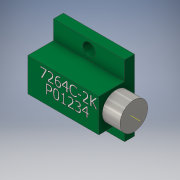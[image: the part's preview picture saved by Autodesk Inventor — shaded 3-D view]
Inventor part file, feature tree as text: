
AUTODESK INVENTOR PART (.ipt)
format: ipt  version: 2016 (Build 200138000, 138)  size: 567,808 bytes
history: native  units: in
note: dims shown in document units (in); Inventor stores cm internally (conversion verified against a paired STEP export)
features: sketch x6, extrude x3, emboss x1, other x1
ambient origin geometry x8: Origin, YZ Plane, XZ Plane, XY Plane, X Axis, Y Axis, Z Axis, Center Point
bodies: Solid1 (feature_tree)
feature tree (11):
  extrude  "Extrusion1"  Depth=0.4in
  extrude  "Extrusion2"  Depth=0.05in
  extrude  "Extrusion3"  Depth=0.188in
  emboss  "Emboss1"
  sketch  "Sketch6"  dims[d10=0.156in]
  sketch  "Sketch7"  dims[d11=0.103in d12=0.1in d13=0.0in d14=0.001in d15=0.0in d20=0.12in d21=0.01in]
  other  "Center of Seismic Mass"
  sketch  "Sketch1"  dims[d1=0.4in d2=0.4in]
  sketch  "Sketch2"  dims[d3=0.071in d4=0.05in]
  sketch  "Sketch3"  dims[d5=0.055in d6=0.0in d7=0.188in]
  sketch  "Sketch4"  dims[d8=0.145in d9=0.0in]
